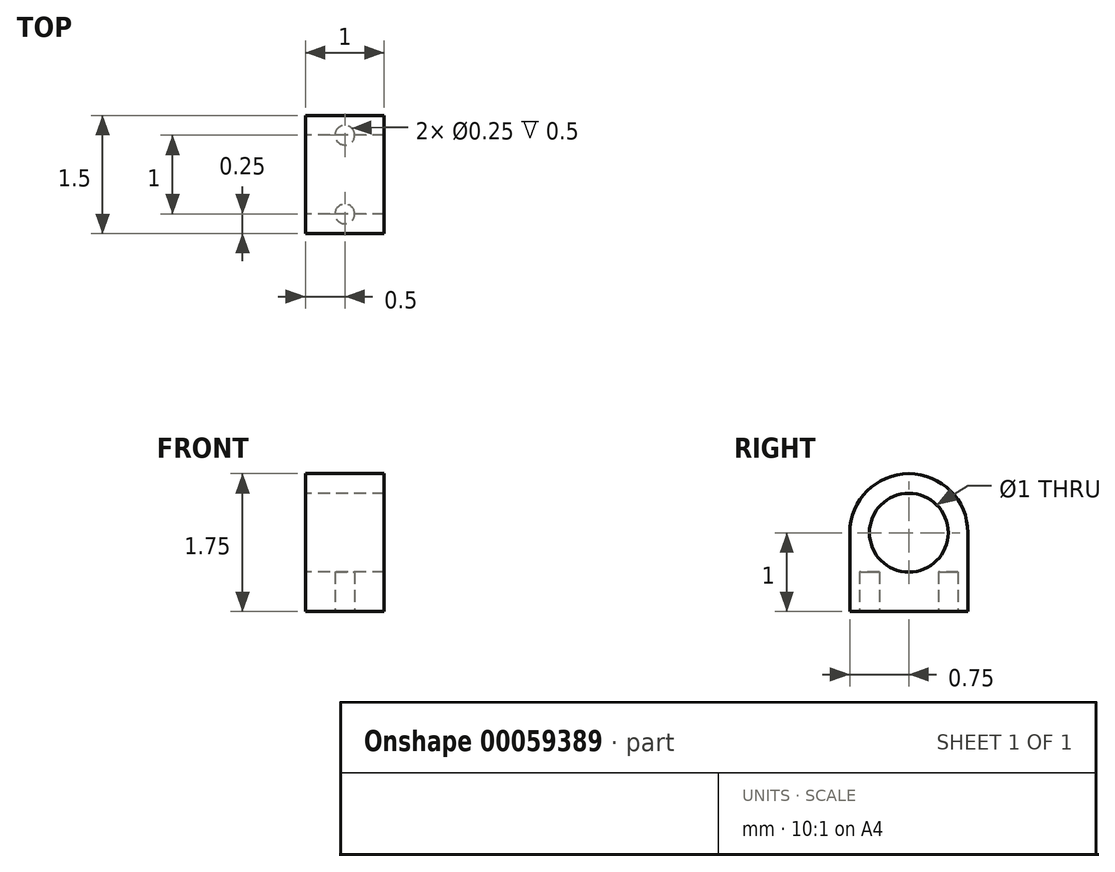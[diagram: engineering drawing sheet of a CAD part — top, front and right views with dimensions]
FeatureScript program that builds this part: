
annotation { "Feature Type Name" : "Feature", "Feature Type Description" : "" }
export const myFeature = defineFeature(function(context is Context, id is Id, definition is map)
    precondition{}
    {
        {
            var Q0;
            Q0=qCreatedBy(makeId("Right.planeOp"),FACE);
            var sketch = newSketch(context, id + "F0", { "sketchPlane" : qUnion([Q0])});
            skCircle(sketch, "E0", {"center": v(0, 0) * mm, "radius": 0.5 * mm});
            skArc(sketch, "E1", {"start": v(0.75, 0) * mm, "mid": v(0, 0.75) * mm, "end": v(-0.75, 0) * mm});
            skLineSegment(sketch, "E2", {"start": v(-0.75, 0) * mm, "end": v(-0.75, -1) * mm});
            skLineSegment(sketch, "E3", {"start": v(-0.75, -1) * mm, "end": v(0.75, -1) * mm});
            skLineSegment(sketch, "E4", {"start": v(0.75, -1) * mm, "end": v(0.75, 0) * mm});
            skSolve(sketch);
        }
        {
            var Q0;
            Q0=makeQuery(id+"F0.imprint","IMPRINT",FACE,{"disambiguationData":[TD([[makeQuery(id+"F0.imprint","IMPRINT",EDGE,{"derivedFrom":sQuery(id+"F0.wireOp",EDGE,"E0")}),-1.0]])]});
            extrude(context, id + "F1", {"entities" : qUnion([Q0]), "endBound" : BoundingType.SYMMETRIC, "depth" : 1 * mm});
        }
        {
            var Q0;
            Q0=makeQuery(id+"F1.opExtrude","SWEPT_FACE",FACE,{"disambiguationData":[OSD([sQuery(id+"F0.wireOp",EDGE,"E3")])]});
            var sketch = newSketch(context, id + "F2", { "sketchPlane" : qUnion([Q0])});
            skCircle(sketch, "E5", {"center": v(0, 0.5) * mm, "radius": 0.12 * mm});
            skCircle(sketch, "E6", {"center": v(0, -0.5) * mm, "radius": 0.12 * mm});
            skSolve(sketch);
        }
        {
            var Q0;
            Q0=makeQuery(id+"F2.imprint","IMPRINT",FACE,{"disambiguationData":[TD([[makeQuery(id+"F2.imprint","IMPRINT",EDGE,{"derivedFrom":sQuery(id+"F2.wireOp",EDGE,"E5")}),1.0]])]});
            var Q1;
            Q1=makeQuery(id+"F2.imprint","IMPRINT",FACE,{"disambiguationData":[TD([[makeQuery(id+"F2.imprint","IMPRINT",EDGE,{"derivedFrom":sQuery(id+"F2.wireOp",EDGE,"E6")}),1.0]])]});
            extrude(context, id + "F3", {"entities" : qUnion([Q0, Q1]), "operationType" : NewBodyOperationType.REMOVE, "oppositeDirection" : true, "depth" : 0.5 * mm});
        }
    });
